# Revit family: Haworth_PopUp_RaceTrack_Table_EU_PRELIMINARY
name_source: partatom
category: Furniture
revit_build: Autodesk Revit 2018 (Build: 20170223_1515(x64)
units: mm (PartAtom-declared; Revit-internal decimal feet)

## family parameters
Always vertical = Yes
Cut with Voids When Loaded = No
OmniClass Number = 23.40.70.14.64.21
OmniClass Title = Systems Furniture
Room Calculation Point = No
Shared = No
Work Plane-Based = No

## types (4) — shared parameters
Assembly Code = E2020200
Caster Finish = Haworth _ Paint _ Metallic Gunmetal
Casters = Yes
Custom Size = No
Description = Haworth - PopUp - RaceTrack Table
Glides = No
Manufacturer = Haworth
Max. Depth = 75 cm
Max. Width = 180 cm
Min. Depth = 45 cm
Min. Width = 120 cm
Min/Max Depth = 46, 60, 76 cm
Min/Max Height = 91.5, 104 cm
Min/Max Width = 120, 140, 160, 180 cm
Model = TPRTXXXX
Revision Number = 1
Size = Verify Final Dim. w/ Haworth
Support Offset = 25 cm
Table Thickness = 3 cm
URL = https://www.haworth.com
URL - Product = https://www.haworth.com
Warranty = http://www.haworth.com

## per-type parameters (varying)
| type | Actual Depth | Actual Height | Actual Width | Depth | High | Large | Leg Height | Low | Plate Depth | Small | Table Radius | Top Width | Width |
| 180 x 76 x 104 | 75 cm | 104 cm | 180 cm | 76 cm | Yes | Yes | 101 cm | No | 40 cm | No | 38 cm | 34 cm | 180 cm |
| 120 x 46 x 91.5 | 46 cm | 92 cm | 120 cm | 46 cm | No | No | 89 cm | Yes | 11 cm | Yes | 23 cm | 20 cm | 120 cm |
| 140 x 60 x 91.5 | 60 cm | 104 cm | 140 cm | 60 cm | Yes | Yes | 101 cm | No | 25 cm | No | 30 cm | 27 cm | 140 cm |
| 160 x 76 x 91.5 | 75 cm | 92 cm | 160 cm | 76 cm | No | Yes | 89 cm | Yes | 40 cm | No | 38 cm | 34 cm | 160 cm |

## geometry (parser evidence)
native form markers: Sweep x12
no freeform markers — native parametric forms only
